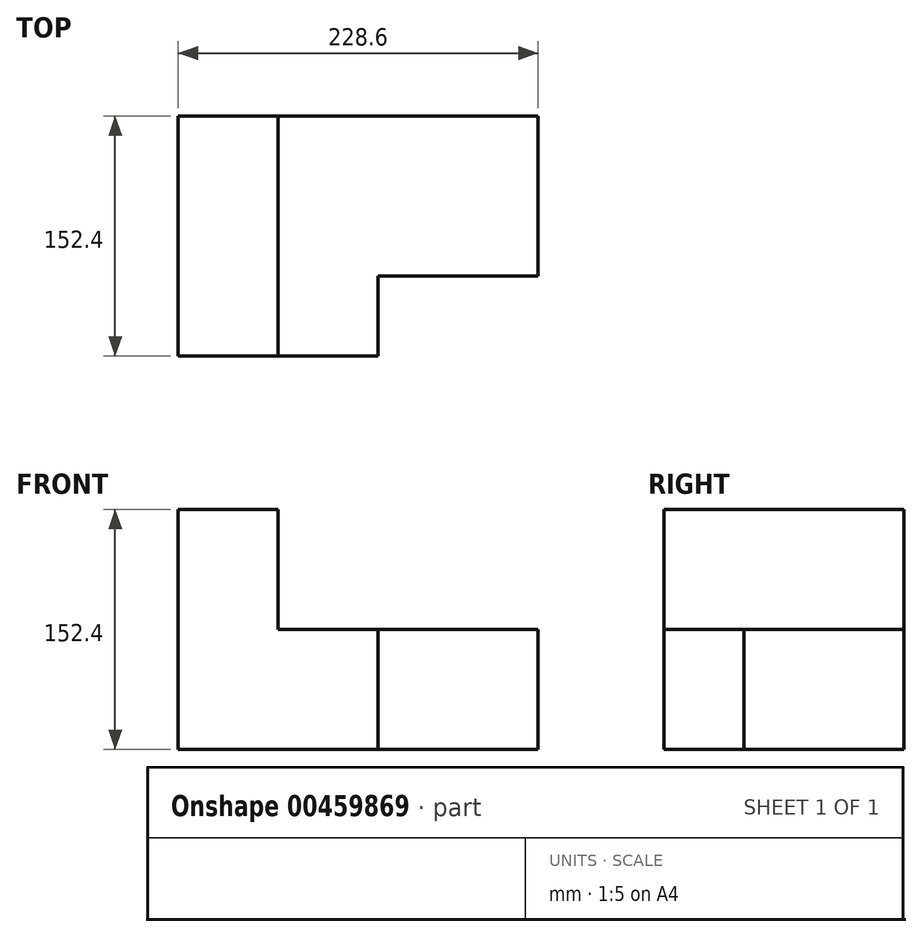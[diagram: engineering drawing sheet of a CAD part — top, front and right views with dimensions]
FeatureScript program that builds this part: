
annotation { "Feature Type Name" : "Feature", "Feature Type Description" : "" }
export const myFeature = defineFeature(function(context is Context, id is Id, definition is map)
    precondition{}
    {
        {
            var Q0;
            Q0=qCreatedBy(makeId("Front.planeOp"),FACE);
            var sketch = newSketch(context, id + "F0", { "sketchPlane" : qUnion([Q0])});
            skLineSegment(sketch, "E0", {"start": v(0, 0) * mm, "end": v(-228.6, 0) * mm});
            skLineSegment(sketch, "E1", {"start": v(-228.6, 0) * mm, "end": v(-228.6, 152.4) * mm});
            skLineSegment(sketch, "E2", {"start": v(-228.6, 152.4) * mm, "end": v(-165.1, 152.4) * mm});
            skLineSegment(sketch, "E3", {"start": v(-165.1, 152.4) * mm, "end": v(-165.1, 76.2) * mm});
            skLineSegment(sketch, "E4", {"start": v(-165.1, 76.2) * mm, "end": v(0, 76.2) * mm});
            skLineSegment(sketch, "E5", {"start": v(0, 76.2) * mm, "end": v(0, 0) * mm});
            skSolve(sketch);
        }
        {
            var Q0;
            Q0=makeQuery(id+"F0.imprint","IMPRINT",FACE,{"disambiguationData":[TD([[makeQuery(id+"F0.imprint","IMPRINT",EDGE,{"derivedFrom":sQuery(id+"F0.wireOp",EDGE,"E0")}),-1.0]])]});
            extrude(context, id + "F1", {"entities" : qUnion([Q0]), "depth" : 152.4 * mm});
        }
        {
            var Q0;
            Q0=makeQuery(id+"F1.opExtrude","CAP_FACE",FACE,{"disambiguationData":[OSD([sQuery(id+"F0.wireOp",EDGE,"E0"),sQuery(id+"F0.wireOp",EDGE,"E1"),sQuery(id+"F0.wireOp",EDGE,"E2"),sQuery(id+"F0.wireOp",EDGE,"E3"),sQuery(id+"F0.wireOp",EDGE,"E4"),sQuery(id+"F0.wireOp",EDGE,"E5")])],"isStart":false});
            var sketch = newSketch(context, id + "F2", { "sketchPlane" : qUnion([Q0])});
            skLineSegment(sketch, "E6", {"start": v(-101.6, 76.2) * mm, "end": v(-101.6, 0) * mm});
            skSolve(sketch);
        }
        {
            var Q0;
            {var subQ0=sQuery(id+"F2.wireOp",EDGE,"E6");Q0=makeQuery(id+"F2.imprint","IMPRINT",FACE,{"disambiguationData":[TD([[makeQuery(id+"F2.imprint","IMPRINT",EDGE,{"derivedFrom":subQ0}),1.0]])]});}
            extrude(context, id + "F3", {"entities" : qUnion([Q0]), "operationType" : NewBodyOperationType.REMOVE, "oppositeDirection" : true, "depth" : 50.8 * mm});
        }
    });
